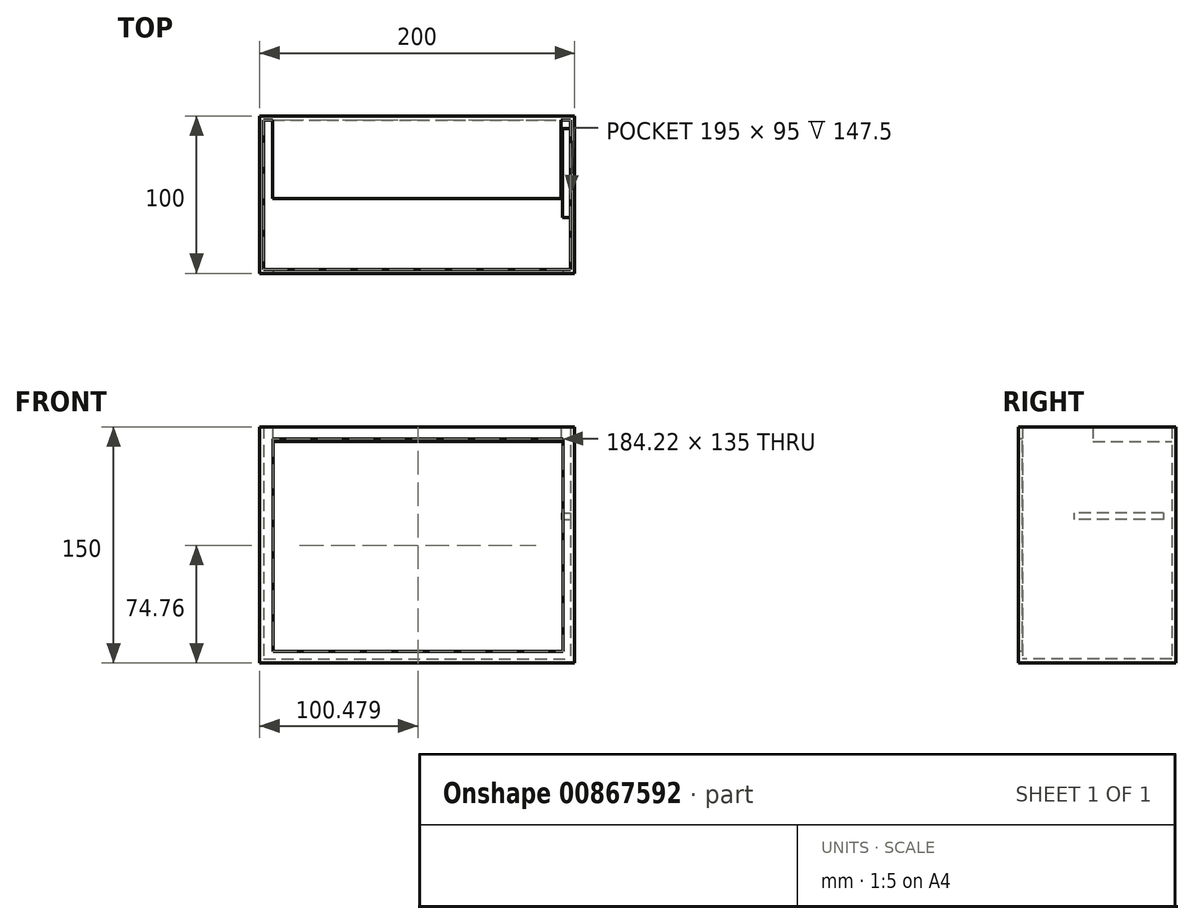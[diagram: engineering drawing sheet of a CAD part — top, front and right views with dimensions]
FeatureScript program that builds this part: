
annotation { "Feature Type Name" : "Feature", "Feature Type Description" : "" }
export const myFeature = defineFeature(function(context is Context, id is Id, definition is map)
    precondition{}
    {
        {
            var Q0;
            Q0=qCreatedBy(makeId("Top.planeOp"),FACE);
            var sketch = newSketch(context, id + "F0", { "sketchPlane" : qUnion([Q0])});
            skLineSegment(sketch, "E0.bottom", {"start": v(-100, 50) * mm, "end": v(100, 50) * mm});
            skLineSegment(sketch, "E0.top", {"start": v(-100, -50) * mm, "end": v(100, -50) * mm});
            skLineSegment(sketch, "E0.left", {"start": v(-100, 50) * mm, "end": v(-100, -50) * mm});
            skLineSegment(sketch, "E0.right", {"start": v(100, 50) * mm, "end": v(100, -50) * mm});
            skPoint(sketch, "E0.middle", {"position": v(0, 0) * mm});
            skSolve(sketch);
        }
        {
            var Q0;
            Q0=makeQuery(id+"F0.imprint","IMPRINT",FACE,{"disambiguationData":[TD([[makeQuery(id+"F0.imprint","IMPRINT",EDGE,{"derivedFrom":sQuery(id+"F0.wireOp",EDGE,"E0.bottom")}),-1.0]])]});
            extrude(context, id + "F1", {"entities" : qUnion([Q0]), "depth" : 150 * mm, "offsetDistance" : 25 * mm});
        }
        {
            var Q0;
            Q0=makeQuery(id+"F1.opExtrude","CAP_FACE",FACE,{"disambiguationData":[OSD([sQuery(id+"F0.wireOp",EDGE,"E0.bottom"),sQuery(id+"F0.wireOp",EDGE,"E0.top"),sQuery(id+"F0.wireOp",EDGE,"E0.left"),sQuery(id+"F0.wireOp",EDGE,"E0.right")])],"isStart":false});
            shell(context, id + "F2", {"entities" : qUnion([Q0]), "thickness" : 2.5 * mm});
        }
        {
            var Q0;
            Q0=makeQuery(id+"F1.opExtrude","SWEPT_FACE",FACE,{"disambiguationData":[OSD([sQuery(id+"F0.wireOp",EDGE,"E0.top")])]});
            var sketch = newSketch(context, id + "F3", { "sketchPlane" : qUnion([Q0])});
            skLineSegment(sketch, "E1.bottom", {"start": v(-91.63, 142.26) * mm, "end": v(92.59, 142.26) * mm});
            skLineSegment(sketch, "E1.top", {"start": v(-91.63, 7.26) * mm, "end": v(92.59, 7.26) * mm});
            skLineSegment(sketch, "E1.left", {"start": v(-91.63, 142.26) * mm, "end": v(-91.63, 7.26) * mm});
            skLineSegment(sketch, "E1.right", {"start": v(92.59, 142.26) * mm, "end": v(92.59, 7.26) * mm});
            skSolve(sketch);
        }
        {
            var Q0;
            Q0 = qSketchRegion(id + "F3", true);
            extrude(context, id + "F4", {"entities" : qUnion([Q0]), "operationType" : NewBodyOperationType.REMOVE, "oppositeDirection" : true, "depth" : 25 * mm, "offsetDistance" : 25 * mm});
        }
        {
            var Q0;
            Q0=makeQuery(id+"F2.opShell","OFFSET_FACE",FACE,{"disambiguationData":[OSD([sQuery(id+"F0.wireOp",EDGE,"E0.right")])]});
            var sketch = newSketch(context, id + "F5", { "sketchPlane" : qUnion([Q0])});
            skLineSegment(sketch, "E2.bottom", {"start": v(-42.12, 95.43) * mm, "end": v(14.6, 95.43) * mm});
            skLineSegment(sketch, "E2.top", {"start": v(-42.12, 91.23) * mm, "end": v(14.6, 91.23) * mm});
            skLineSegment(sketch, "E2.left", {"start": v(-42.12, 95.43) * mm, "end": v(-42.12, 91.23) * mm});
            skLineSegment(sketch, "E2.right", {"start": v(14.6, 95.43) * mm, "end": v(14.6, 91.23) * mm});
            skSolve(sketch);
        }
        {
            var Q0;
            Q0 = qSketchRegion(id + "F5", true);
            extrude(context, id + "F6", {"entities" : qUnion([Q0]), "operationType" : NewBodyOperationType.ADD, "depth" : 5 * mm, "offsetDistance" : 25 * mm});
        }
        {
            var Q0;
            Q0=makeQuery(id+"F2.opShell","OFFSET_FACE",FACE,{"disambiguationData":[OSD([sQuery(id+"F0.wireOp",EDGE,"E0.bottom")])]});
            var sketch = newSketch(context, id + "F7", { "sketchPlane" : qUnion([Q0])});
            skLineSegment(sketch, "E3.bottom", {"start": v(-91.74, 150) * mm, "end": v(91.26, 150) * mm});
            skLineSegment(sketch, "E3.top", {"start": v(-91.74, 140.69) * mm, "end": v(91.26, 140.69) * mm});
            skLineSegment(sketch, "E3.left", {"start": v(-91.74, 150) * mm, "end": v(-91.74, 140.69) * mm});
            skLineSegment(sketch, "E3.right", {"start": v(91.26, 150) * mm, "end": v(91.26, 140.69) * mm});
            skSolve(sketch);
        }
        {
            var Q0;
            Q0 = qSketchRegion(id + "F7", true);
            extrude(context, id + "F8", {"entities" : qUnion([Q0]), "operationType" : NewBodyOperationType.ADD, "depth" : 50 * mm, "offsetDistance" : 25 * mm});
        }
    });
